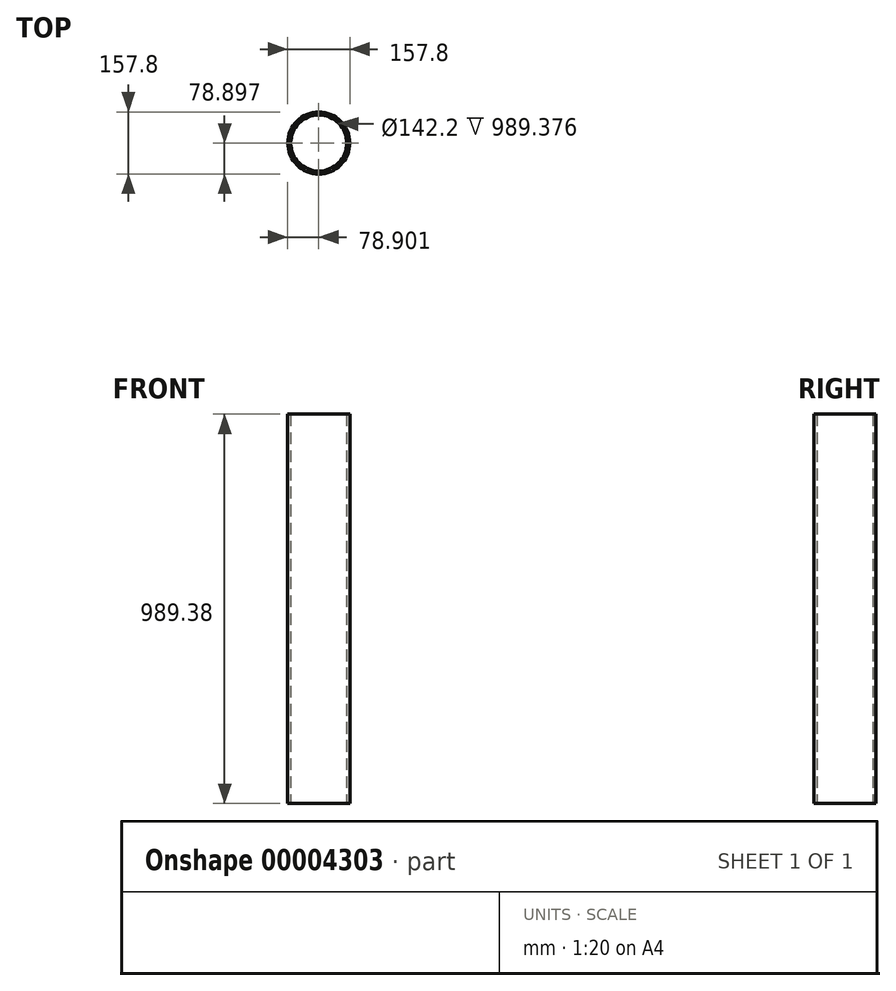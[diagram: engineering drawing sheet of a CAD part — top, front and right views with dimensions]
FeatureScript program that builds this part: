
annotation { "Feature Type Name" : "Feature", "Feature Type Description" : "" }
export const myFeature = defineFeature(function(context is Context, id is Id, definition is map)
    precondition{}
    {
        {
            var Q0;
            Q0=qCreatedBy(makeId("Top.planeOp"),FACE);
            var sketch = newSketch(context, id + "F0", { "sketchPlane" : qUnion([Q0])});
            skCircle(sketch, "E0", {"center": v(-22.32, 17.19) * mm, "radius": 78.9 * mm});
            skCircle(sketch, "E1.0", {"center": v(-22.32, 17.19) * mm, "radius": 71.1 * mm});
            skSolve(sketch);
        }
        {
            var Q0;
            Q0=makeQuery(id+"F0.imprint","IMPRINT",FACE,{"disambiguationData":[TD([[makeQuery(id+"F0.imprint","IMPRINT",EDGE,{"derivedFrom":sQuery(id+"F0.wireOp",EDGE,"E0")}),1.0]])]});
            extrude(context, id + "F1", {"entities" : qUnion([Q0]), "endBound" : BoundingType.SYMMETRIC, "depth" : 989.38 * mm});
        }
    });
